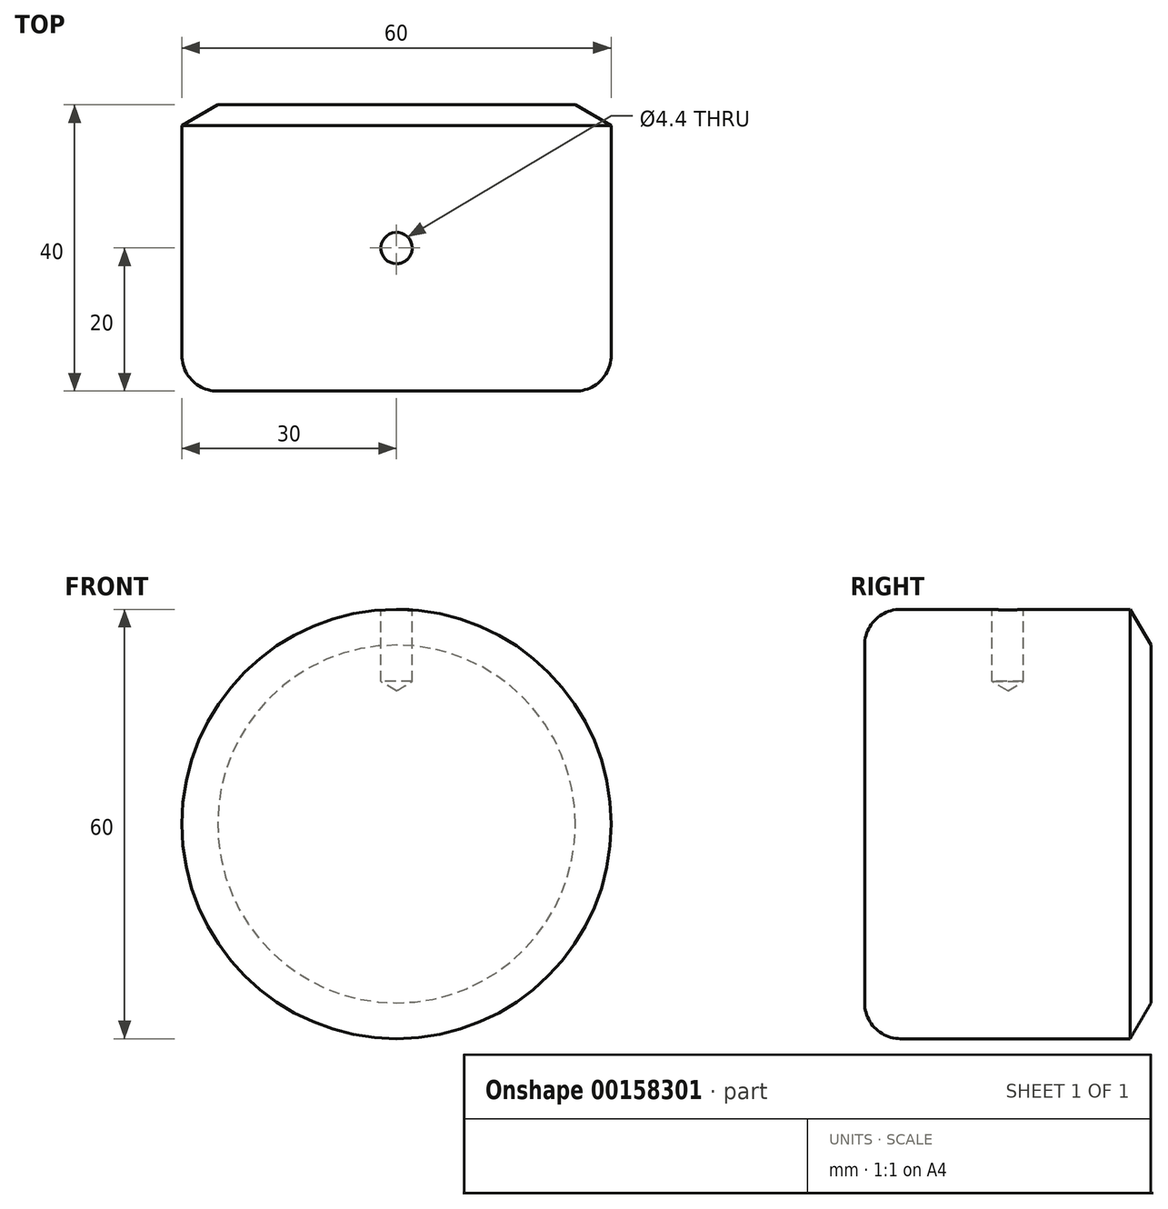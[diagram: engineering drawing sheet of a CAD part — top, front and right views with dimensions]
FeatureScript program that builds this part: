
annotation { "Feature Type Name" : "Feature", "Feature Type Description" : "" }
export const myFeature = defineFeature(function(context is Context, id is Id, definition is map)
    precondition{}
    {
        {
            assignVariable(context, id + "F0", {"name" : "th", "anyValue" : 40});
        }
        {
            assignVariable(context, id + "F1", {"name" : "r", "anyValue" : 30});
        }
        {
            var Q0;
            Q0=qCreatedBy(makeId("Front.planeOp"),FACE);
            var sketch = newSketch(context, id + "F2", { "sketchPlane" : qUnion([Q0])});
            skPoint(sketch, "E0", {"position": v(30, 0) * mm});
            skCircle(sketch, "E1", {"center": v(0, 0) * mm, "radius": 30 * mm});
            skSolve(sketch);
        }
        {
            var Q0;
            Q0=makeQuery(id+"F2.imprint","IMPRINT",FACE,{"disambiguationData":[TD([[makeQuery(id+"F2.imprint","IMPRINT",EDGE,{"derivedFrom":sQuery(id+"F2.wireOp",EDGE,"E1")}),1.0]])]});
            extrude(context, id + "F3", {"entities" : qUnion([Q0]), "endBound" : BoundingType.SYMMETRIC, "depth" : (getVariable(context, 'th')) * mm});
        }
        {
            var Q0;
            Q0=qCreatedBy(makeId("Top.planeOp"),FACE);
            cPlane(context, id + "F4", {"entities" : qUnion([Q0]), "cplaneType" : CPlaneType.OFFSET, "offset" : (getVariable(context, 'r')) * mm, "width" : 150 * mm, "height" : 150 * mm});
        }
        {
            var Q0;
            Q0=qCreatedBy(id+"F4.planeOp",FACE);
            var sketch = newSketch(context, id + "F5", { "sketchPlane" : qUnion([Q0])});
            skPoint(sketch, "E2", {"position": v(0, 0) * mm});
            skSolve(sketch);
        }
        {
            var Q0;
            Q0=makeQuery(id+"F3.opExtrude","CAP_EDGE",EDGE,{"disambiguationData":[OSD([sQuery(id+"F2.wireOp",EDGE,"E1")])],"isStart":false});
            fillet(context, id + "F6", {"entities" : qUnion([Q0]), "radius" : 5 * mm, "tangentPropagation" : true, "allowEdgeOverflow" : false});
        }
        {
            var Q0;
            Q0=sQuery(id+"F5.wireOp",VERTEX,"E2");
            var Q1;
            Q1=makeQuery(id+"F3.opExtrude","SWEPT_BODY",BODY,{"disambiguationData":[OSD([sQuery(id+"F2.wireOp",EDGE,"E1")])]});
            hole(context, id + "F7", {"style" : HoleStyle.SIMPLE, "endStyle" : HoleEndStyle.BLIND, "standardTappedOrClearance" : lookupTablePath({ "standard" : "ISO", "fit" : "Normal", "size" : "M4", "type" : "Clearance" }), "standardBlindInLast" : lookupTablePath({ "fit" : "Standard", "standard" : "ISO", "size" : "M4", "type" : "Clearance" }), "holeDiameter" : 4.4 * mm, "holeDepth" : 10 * mm, "locations" : qUnion([Q0]), "scope" : qUnion([Q1])});
        }
        {
            var Q0;
            Q0=makeQuery(id+"F3.opExtrude","CAP_FACE",FACE,{"disambiguationData":[OSD([sQuery(id+"F2.wireOp",EDGE,"E1")])],"isStart":true});
            chamfer(context, id + "F8", {"entities" : qUnion([Q0]), "chamferType" : ChamferType.OFFSET_ANGLE, "width" : 5 * mm, "oppositeDirection" : true, "angle" : 30 * degree, "tangentPropagation" : true});
        }
    });
